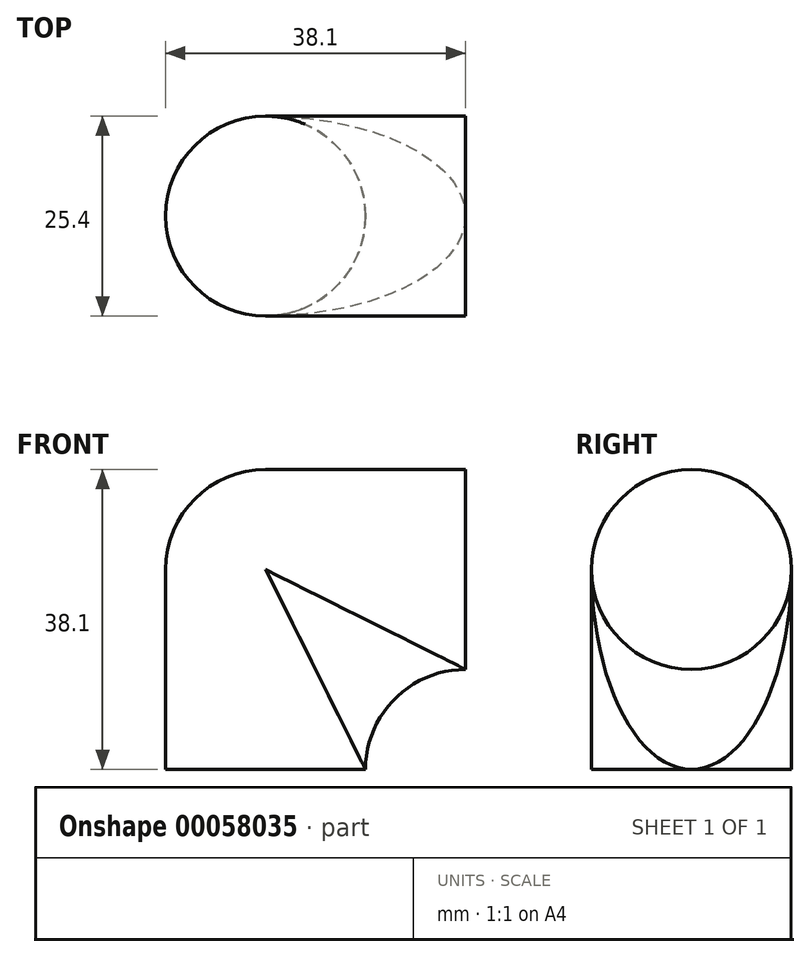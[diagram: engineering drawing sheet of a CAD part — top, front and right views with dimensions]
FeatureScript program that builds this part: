
annotation { "Feature Type Name" : "Feature", "Feature Type Description" : "" }
export const myFeature = defineFeature(function(context is Context, id is Id, definition is map)
    precondition{}
    {
        {
            var Q0;
            Q0=qCreatedBy(makeId("Top.planeOp"),FACE);
            var sketch = newSketch(context, id + "F0", { "sketchPlane" : qUnion([Q0])});
            skCircle(sketch, "E0", {"center": v(0, 0) * mm, "radius": 12.7 * mm});
            skSolve(sketch);
        }
        {
            var Q0;
            Q0=qCreatedBy(makeId("Front.planeOp"),FACE);
            var sketch = newSketch(context, id + "F1", { "sketchPlane" : qUnion([Q0])});
            skLineSegment(sketch, "E1", {"start": v(0, 0) * mm, "end": v(0, 25.4) * mm});
            skLineSegment(sketch, "E2", {"start": v(0, 25.4) * mm, "end": v(25.4, 25.4) * mm});
            skSolve(sketch);
        }
        {
            var Q0;
            Q0=makeQuery(id+"F0.imprint","IMPRINT",FACE,{"disambiguationData":[TD([[makeQuery(id+"F0.imprint","IMPRINT",EDGE,{"derivedFrom":sQuery(id+"F0.wireOp",EDGE,"E0")}),1.0]])]});
            var Q1;
            Q1=sQuery(id+"F1.wireOp",EDGE,"E1");
            var Q2;
            Q2=sQuery(id+"F1.wireOp",EDGE,"E2");
            sweep(context, id + "F2", {"profiles" : qUnion([Q0]), "path" : qUnion([Q1, Q2])});
        }
        {
            var Q0;
            Q0=makeQuery(id+"F2.opSweep","MID_CAP_EDGE",EDGE,{"disambiguationData":[OSD([sQuery(id+"F0.wireOp",EDGE,"E0"),sQuery(id+"F1.wireOp",VERTEX,"E2.start")])],"capPos":1.0});
            fillet(context, id + "F3", {"entities" : qUnion([Q0]), "radius" : 12.7 * mm, "tangentPropagation" : true, "allowEdgeOverflow" : false});
        }
    });
